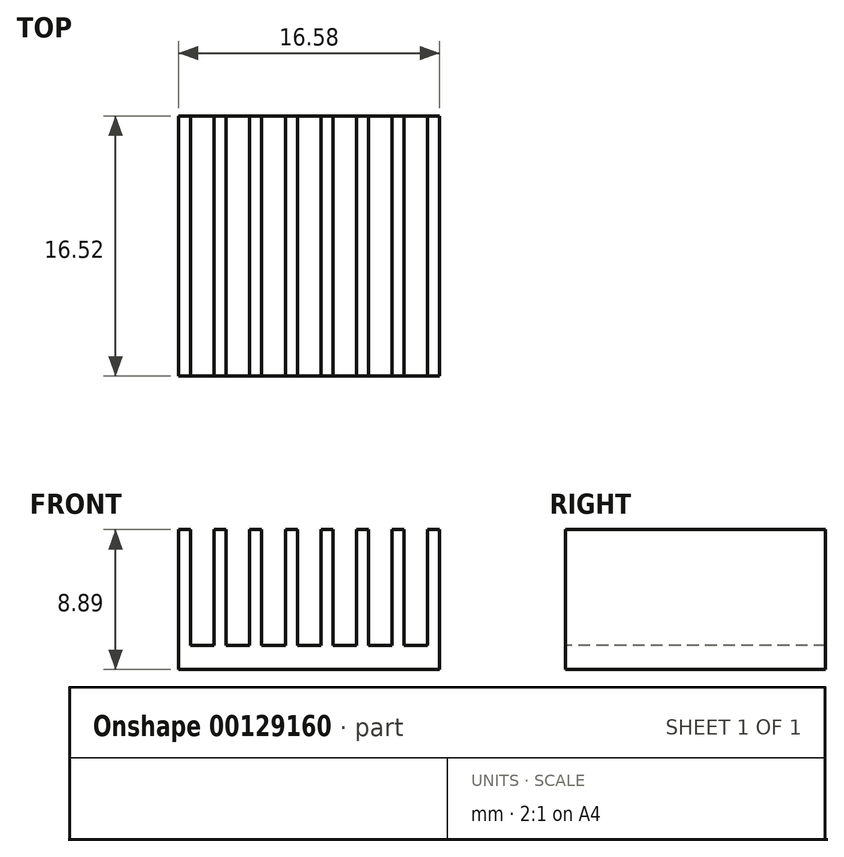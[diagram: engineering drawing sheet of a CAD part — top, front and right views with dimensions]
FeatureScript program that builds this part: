
annotation { "Feature Type Name" : "Feature", "Feature Type Description" : "" }
export const myFeature = defineFeature(function(context is Context, id is Id, definition is map)
    precondition{}
    {
        {
            var Q0;
            Q0=qCreatedBy(makeId("Top.planeOp"),FACE);
            var sketch = newSketch(context, id + "F0", { "sketchPlane" : qUnion([Q0])});
            skLineSegment(sketch, "E0.bottom", {"start": v(-8.3, 8.26) * mm, "end": v(8.3, 8.26) * mm});
            skLineSegment(sketch, "E0.top", {"start": v(-8.3, -8.26) * mm, "end": v(8.3, -8.26) * mm});
            skLineSegment(sketch, "E0.left", {"start": v(-8.3, 8.26) * mm, "end": v(-8.3, -8.26) * mm});
            skLineSegment(sketch, "E0.right", {"start": v(8.3, 8.26) * mm, "end": v(8.3, -8.26) * mm});
            skSolve(sketch);
        }
        {
            var Q0;
            Q0 = qSketchRegion(id + "F0", true);
            extrude(context, id + "F1", {"entities" : qUnion([Q0]), "depth" : 8.9 * mm});
        }
        {
            var Q0;
            Q0=makeQuery(id+"F1.opExtrude","SWEPT_FACE",FACE,{"disambiguationData":[OSD([sQuery(id+"F0.wireOp",EDGE,"E0.top")])]});
            var sketch = newSketch(context, id + "F2", { "sketchPlane" : qUnion([Q0])});
            skLineSegment(sketch, "E1.bottom", {"start": v(-0.75, 8.9) * mm, "end": v(0.75, 8.9) * mm});
            skLineSegment(sketch, "E1.top", {"start": v(-0.75, 1.52) * mm, "end": v(0.75, 1.52) * mm});
            skLineSegment(sketch, "E1.left", {"start": v(-0.75, 8.9) * mm, "end": v(-0.75, 1.52) * mm});
            skLineSegment(sketch, "E1.right", {"start": v(0.75, 8.9) * mm, "end": v(0.75, 1.52) * mm});
            skLineSegment(sketch, "E2.bottom", {"start": v(1.51, 8.9) * mm, "end": v(3, 8.9) * mm});
            skLineSegment(sketch, "E2.top", {"start": v(1.51, 1.52) * mm, "end": v(3, 1.52) * mm});
            skLineSegment(sketch, "E2.left", {"start": v(1.51, 8.9) * mm, "end": v(1.51, 1.52) * mm});
            skLineSegment(sketch, "E2.right", {"start": v(3, 8.9) * mm, "end": v(3, 1.52) * mm});
            skLineSegment(sketch, "E3.bottom", {"start": v(3.77, 8.9) * mm, "end": v(5.27, 8.9) * mm});
            skLineSegment(sketch, "E3.top", {"start": v(3.77, 1.52) * mm, "end": v(5.27, 1.52) * mm});
            skLineSegment(sketch, "E3.left", {"start": v(3.77, 8.9) * mm, "end": v(3.77, 1.52) * mm});
            skLineSegment(sketch, "E3.right", {"start": v(5.27, 8.9) * mm, "end": v(5.27, 1.52) * mm});
            skLineSegment(sketch, "E4.bottom", {"start": v(6.03, 8.9) * mm, "end": v(7.53, 8.9) * mm});
            skLineSegment(sketch, "E4.top", {"start": v(6.03, 1.52) * mm, "end": v(7.53, 1.52) * mm});
            skLineSegment(sketch, "E4.left", {"start": v(6.03, 8.9) * mm, "end": v(6.03, 1.52) * mm});
            skLineSegment(sketch, "E4.right", {"start": v(7.53, 8.9) * mm, "end": v(7.53, 1.52) * mm});
            skLineSegment(sketch, "E5.MirrorCS", {"start": v(-1.51, 8.9) * mm, "end": v(-1.51, 1.52) * mm});
            skLineSegment(sketch, "E6.MirrorCS", {"start": v(-1.51, 1.52) * mm, "end": v(-3, 1.52) * mm});
            skLineSegment(sketch, "E7.MirrorCS", {"start": v(-1.51, 8.9) * mm, "end": v(-3, 8.9) * mm});
            skLineSegment(sketch, "E8.MirrorCS", {"start": v(-3, 8.9) * mm, "end": v(-3, 1.52) * mm});
            skLineSegment(sketch, "E9.MirrorCS", {"start": v(-3.77, 8.9) * mm, "end": v(-5.27, 8.9) * mm});
            skLineSegment(sketch, "E10.MirrorCS", {"start": v(-3.77, 1.52) * mm, "end": v(-5.27, 1.52) * mm});
            skLineSegment(sketch, "E11.MirrorCS", {"start": v(-3.77, 8.9) * mm, "end": v(-3.77, 1.52) * mm});
            skLineSegment(sketch, "E12.MirrorCS", {"start": v(-7.53, 8.9) * mm, "end": v(-7.53, 1.52) * mm});
            skLineSegment(sketch, "E13.MirrorCS", {"start": v(-6.03, 8.9) * mm, "end": v(-6.03, 1.52) * mm});
            skLineSegment(sketch, "E14.MirrorCS", {"start": v(-6.03, 1.52) * mm, "end": v(-7.53, 1.52) * mm});
            skLineSegment(sketch, "E15.MirrorCS", {"start": v(-6.03, 8.9) * mm, "end": v(-7.53, 8.9) * mm});
            skLineSegment(sketch, "E16.MirrorCS", {"start": v(-5.27, 8.9) * mm, "end": v(-5.27, 1.52) * mm});
            skSolve(sketch);
        }
        {
            var Q0;
            Q0 = qSketchRegion(id + "F2", true);
            extrude(context, id + "F3", {"entities" : qUnion([Q0]), "operationType" : NewBodyOperationType.REMOVE, "oppositeDirection" : true, "depth" : 25.4 * mm});
        }
    });
